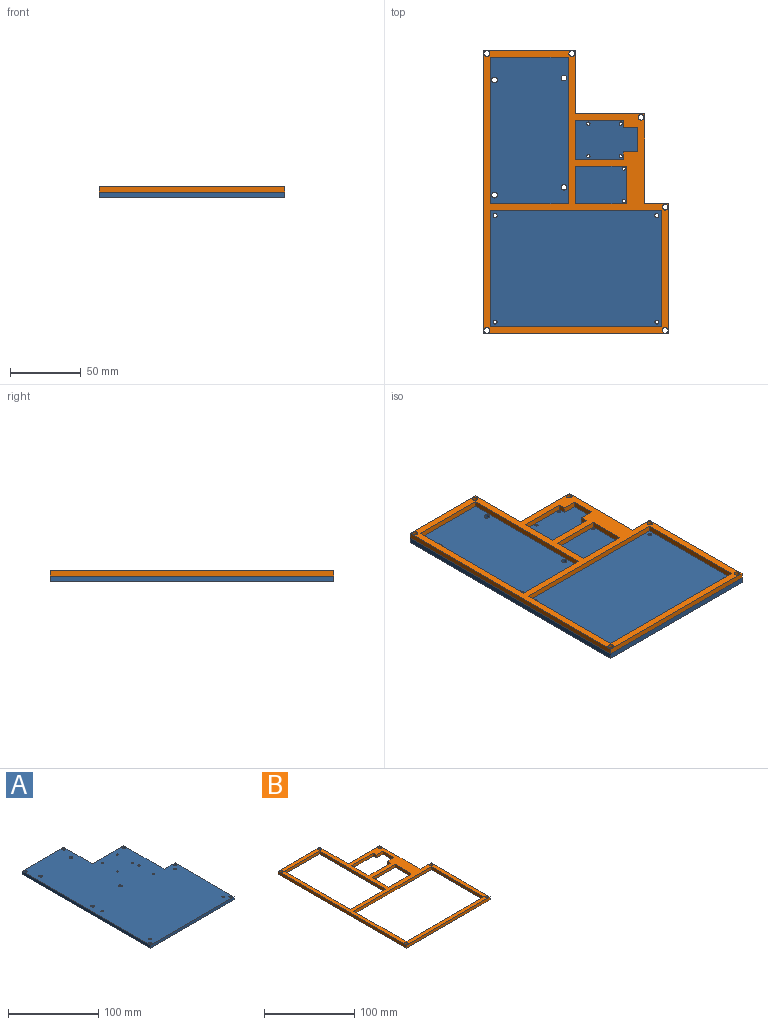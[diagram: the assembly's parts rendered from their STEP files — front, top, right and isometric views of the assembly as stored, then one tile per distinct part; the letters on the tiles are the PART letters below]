
ASSEMBLY  parts=2 mates=1
PART A: 30 faces, bbox 131x200.5x4 mm
  f0: plane 200.5x4mm, normal (-1,0,0), area 802mm2, adj f1,f25,f28,f29
  f1: plane 131x4mm, normal (0,-1,0), area 524mm2, adj f0,f2,f28,f29
  f2: plane 92x4mm, normal (1,0,0), area 368mm2, adj f1,f3,f28,f29
  f3: plane 17x4mm, normal (0,1,0), area 68mm2, adj f2,f4,f28,f29
  f4: plane 63.5x4mm, normal (1,0,0), area 254mm2, adj f3,f5,f28,f29
  f5: plane 49x4mm, normal (0,1,0), area 196mm2, adj f4,f6,f28,f29
  f6: plane 45x4mm, normal (1,0,0), area 180mm2, adj f5,f25,f28,f29
  f7: cylinder r=1.4mm len=4mm, axis (0,0,-1), area 35.2mm2, adj f28,f29
  f8: cylinder r=1.4mm len=4mm, axis (0,0,-1), area 35.2mm2, adj f28,f29
  f9: cylinder r=1.4mm len=4mm, axis (0,0,-1), area 35.2mm2, adj f28,f29
  f10: cylinder r=1.2mm len=4mm, axis (0,0,-1), area 30.2mm2, adj f28,f29
  f11: cylinder r=1.2mm len=4mm, axis (0,0,-1), area 30.2mm2, adj f28,f29
  f12: cylinder r=1.15mm len=4mm, axis (0,0,-1), area 28.9mm2, adj f28,f29
  f13: cylinder r=1.15mm len=4mm, axis (0,0,-1), area 28.9mm2, adj f28,f29
  f14: cylinder r=1.15mm len=4mm, axis (0,0,-1), area 28.9mm2, adj f28,f29
  f15: cylinder r=1.15mm len=4mm, axis (0,0,-1), area 28.9mm2, adj f28,f29
  f16: cylinder r=2mm len=4mm, axis (0,0,-1), area 50.3mm2, adj f28,f29
  f17: cylinder r=2mm len=4mm, axis (0,0,-1), area 50.3mm2, adj f28,f29
  f18: cylinder r=2mm len=4mm, axis (0,0,-1), area 50.3mm2, adj f28,f29
  f19: cylinder r=2mm len=4mm, axis (0,0,-1), area 50.3mm2, adj f28,f29
  f20: cylinder r=2mm len=4mm, axis (0,0,-1), area 50.3mm2, adj f28,f29
  f21: cylinder r=2mm len=4mm, axis (0,0,-1), area 50.3mm2, adj f28,f29
  f22: cylinder r=2mm len=4mm, axis (0,0,-1), area 50.3mm2, adj f28,f29
  f23: cylinder r=2mm len=4mm, axis (0,0,-1), area 50.3mm2, adj f28,f29
  f24: cylinder r=2mm len=4mm, axis (0,0,-1), area 50.3mm2, adj f28,f29
  f25: plane 65x4mm, normal (0,1,0), area 260mm2, adj f0,f6,f28,f29
  f26: cylinder r=2mm len=4mm, axis (0,0,-1), area 50.3mm2, adj f28,f29
  f27: cylinder r=1.4mm len=4mm, axis (0,0,-1), area 35.2mm2, adj f28,f29
  f28: plane 200.5x131mm, normal (0,0,1), area 22040mm2, adj f0,f1,f2,f3,f4,f5,f6,f7
  f29: plane 200.5x131mm, normal (0,0,-1), area 22040mm2, adj f0,f1,f2,f3,f4,f5,f6,f7
PART B: 36 faces, bbox 131x200.5x4 mm
  f0: plane 36x4mm, normal (0,-1,0), area 144mm2, adj f1,f23,f34,f35
  f1: plane 26.5x4mm, normal (-1,0,0), area 106mm2, adj f0,f2,f34,f35
  f2: plane 36x4mm, normal (0,1,0), area 144mm2, adj f1,f23,f34,f35
  f3: plane 10x4mm, normal (0,-1,0), area 40mm2, adj f4,f24,f34,f35
  f4: plane 17x4mm, normal (-1,0,0), area 68mm2, adj f3,f5,f34,f35
  f5: plane 10x4mm, normal (0,1,0), area 40mm2, adj f4,f6,f34,f35
  f6: plane 5x4mm, normal (-1,0,0), area 20mm2, adj f5,f7,f34,f35
  f7: plane 34x4mm, normal (0,1,0), area 136mm2, adj f6,f8,f34,f35
  f8: plane 27x4mm, normal (1,0,0), area 108mm2, adj f7,f9,f34,f35
  f9: plane 34x4mm, normal (0,-1,0), area 136mm2, adj f8,f24,f34,f35
  f10: plane 55x4mm, normal (0,-1,0), area 220mm2, adj f11,f25,f34,f35
  f11: plane 103.5x4mm, normal (-1,0,0), area 414mm2, adj f10,f12,f34,f35
  f12: plane 55x4mm, normal (0,1,0), area 220mm2, adj f11,f25,f34,f35
  f13: plane 121x4mm, normal (0,-1,0), area 484mm2, adj f14,f26,f34,f35
  f14: plane 82x4mm, normal (-1,0,0), area 328mm2, adj f13,f15,f34,f35
  f15: plane 121x4mm, normal (0,1,0), area 484mm2, adj f14,f26,f34,f35
  f16: plane 200.5x4mm, normal (-1,0,0), area 802mm2, adj f17,f31,f34,f35
  f17: plane 131x4mm, normal (0,-1,0), area 524mm2, adj f16,f18,f34,f35
  f18: plane 92x4mm, normal (1,0,0), area 368mm2, adj f17,f19,f34,f35
  f19: plane 17x4mm, normal (0,1,0), area 68mm2, adj f18,f20,f34,f35
  f20: plane 63.5x4mm, normal (1,0,0), area 254mm2, adj f19,f21,f34,f35
  f21: plane 49x4mm, normal (0,1,0), area 196mm2, adj f20,f22,f34,f35
  f22: plane 45x4mm, normal (1,0,0), area 180mm2, adj f21,f31,f34,f35
  f23: plane 26.5x4mm, normal (1,0,0), area 106mm2, adj f0,f2,f34,f35
  f24: plane 5x4mm, normal (-1,0,0), area 20mm2, adj f3,f9,f34,f35
  f25: plane 103.5x4mm, normal (1,0,0), area 414mm2, adj f10,f12,f34,f35
  f26: plane 82x4mm, normal (1,0,0), area 328mm2, adj f13,f15,f34,f35
  f27: cylinder r=2mm len=4mm, axis (0,0,-1), area 50.3mm2, adj f34,f35
  f28: cylinder r=2mm len=4mm, axis (0,0,-1), area 50.3mm2, adj f34,f35
  f29: cylinder r=2mm len=4mm, axis (0,0,-1), area 50.3mm2, adj f34,f35
  f30: cylinder r=2mm len=4mm, axis (0,0,-1), area 50.3mm2, adj f34,f35
  f31: plane 65x4mm, normal (0,1,0), area 260mm2, adj f16,f22,f34,f35
  f32: cylinder r=2mm len=4mm, axis (0,0,-1), area 50.3mm2, adj f34,f35
  f33: cylinder r=2mm len=4mm, axis (0,0,-1), area 50.3mm2, adj f34,f35
  f34: plane 200.5x131mm, normal (0,0,1), area 4484.1mm2, adj f0,f1,f2,f3,f4,f5,f6,f7
  f35: plane 200.5x131mm, normal (0,0,-1), area 4484.1mm2, adj f0,f1,f2,f3,f4,f5,f6,f7
PLACE A t=(-19.99,50.3,-6.25)mm
PLACE B t=(-19.99,50.3,-2.25)mm
MATE fastened A.f28 <-> B.f35  axis (0,0,1) through (-65.69,-100.52,-2.25)mm
